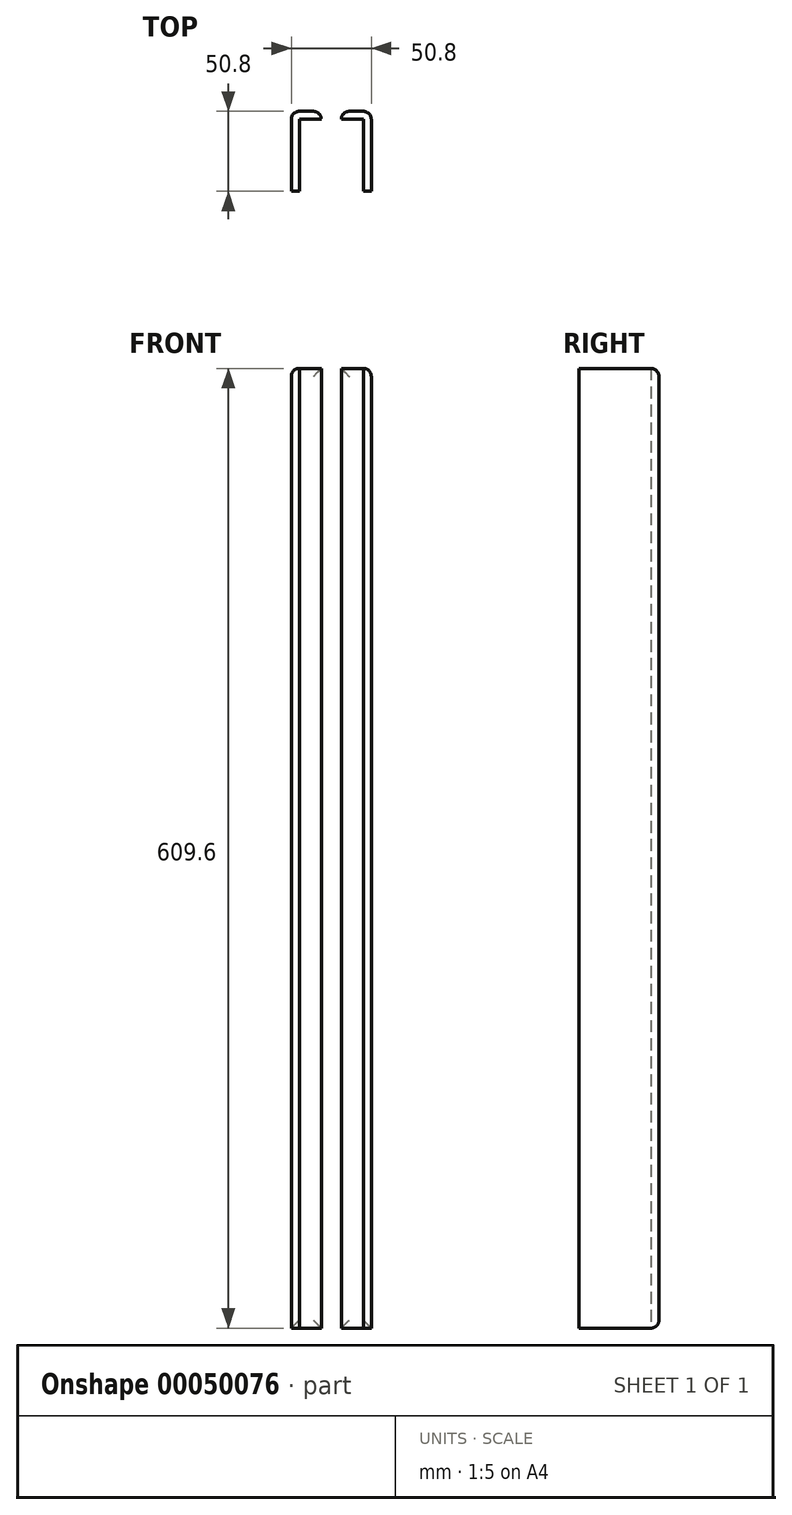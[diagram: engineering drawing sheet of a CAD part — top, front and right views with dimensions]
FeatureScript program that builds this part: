
annotation { "Feature Type Name" : "Feature", "Feature Type Description" : "" }
export const myFeature = defineFeature(function(context is Context, id is Id, definition is map)
    precondition{}
    {
        {
            var Q0;
            Q0=qCreatedBy(makeId("Top.planeOp"),FACE);
            var sketch = newSketch(context, id + "F0", { "sketchPlane" : qUnion([Q0])});
            skLineSegment(sketch, "E0.rect.bottom", {"start": v(25.4, 25.4) * mm, "end": v(6.35, 25.4) * mm});
            skLineSegment(sketch, "E0.rect.top", {"start": v(25.4, -25.4) * mm, "end": v(-25.4, -25.4) * mm});
            skLineSegment(sketch, "E0.rect.left", {"start": v(25.4, 25.4) * mm, "end": v(25.4, -25.4) * mm});
            skLineSegment(sketch, "E0.rect.right", {"start": v(-25.4, 25.4) * mm, "end": v(-25.4, -25.4) * mm});
            skPoint(sketch, "E0.rect.middle", {"position": v(0, 0) * mm});
            skLineSegment(sketch, "E1.rect.top", {"start": v(6.35, 0) * mm, "end": v(-6.35, 0) * mm});
            skLineSegment(sketch, "E1.rect.left", {"start": v(6.35, 25.4) * mm, "end": v(6.35, 0) * mm});
            skLineSegment(sketch, "E1.rect.right", {"start": v(-6.35, 25.4) * mm, "end": v(-6.35, 0) * mm});
            skPoint(sketch, "E1.rect.middle", {"position": v(0, 12.7) * mm});
            skLineSegment(sketch, "E2.trimOffspring", {"start": v(-6.35, 25.4) * mm, "end": v(-25.4, 25.4) * mm});
            skSolve(sketch);
        }
        {
            var Q0;
            Q0=makeQuery(id+"F0.imprint","IMPRINT",FACE,{"disambiguationData":[TD([[makeQuery(id+"F0.imprint","IMPRINT",EDGE,{"derivedFrom":sQuery(id+"F0.wireOp",EDGE,"E0.rect.bottom")}),1.0]])]});
            extrude(context, id + "F1", {"entities" : qUnion([Q0]), "depth" : 609.6 * mm});
        }
        {
            var Q0;
            Q0=makeQuery(id+"F1.opExtrude","SWEPT_FACE",FACE,{"disambiguationData":[OSD([sQuery(id+"F0.wireOp",EDGE,"E2.trimOffspring")])]});
            var Q1;
            Q1=makeQuery(id+"F1.opExtrude","SWEPT_FACE",FACE,{"disambiguationData":[OSD([sQuery(id+"F0.wireOp",EDGE,"E0.rect.bottom")])]});
            fillet(context, id + "F2", {"entities" : qUnion([Q0, Q1]), "radius" : 5.08 * mm, "tangentPropagation" : true, "allowEdgeOverflow" : false});
        }
        {
            var Q0;
            Q0=makeQuery(id+"F1.opExtrude","CAP_EDGE",EDGE,{"disambiguationData":[OSD([sQuery(id+"F0.wireOp",EDGE,"E0.rect.left")])],"isStart":false});
            var Q1;
            Q1=makeQuery(id+"F1.opExtrude","CAP_EDGE",EDGE,{"disambiguationData":[OSD([sQuery(id+"F0.wireOp",EDGE,"E0.rect.right")])],"isStart":false});
            fillet(context, id + "F3", {"entities" : qUnion([Q0, Q1]), "radius" : 5.08 * mm, "tangentPropagation" : true, "allowEdgeOverflow" : false});
        }
        {
            var Q0;
            Q0=makeQuery(id+"F1.opExtrude","CAP_FACE",FACE,{"disambiguationData":[OSD([sQuery(id+"F0.wireOp",EDGE,"E0.rect.bottom"),sQuery(id+"F0.wireOp",EDGE,"E0.rect.top"),sQuery(id+"F0.wireOp",EDGE,"E0.rect.left"),sQuery(id+"F0.wireOp",EDGE,"E0.rect.right"),sQuery(id+"F0.wireOp",EDGE,"E1.rect.top"),sQuery(id+"F0.wireOp",EDGE,"E1.rect.left"),sQuery(id+"F0.wireOp",EDGE,"E1.rect.right"),sQuery(id+"F0.wireOp",EDGE,"E2.trimOffspring")])],"isStart":false});
            extrude(context, id + "F4", {"entities" : qUnion([Q0]), "operationType" : NewBodyOperationType.REMOVE, "endBound" : BoundingType.THROUGH_ALL, "oppositeDirection" : true, "depth" : 25.4 * mm});
        }
    });
